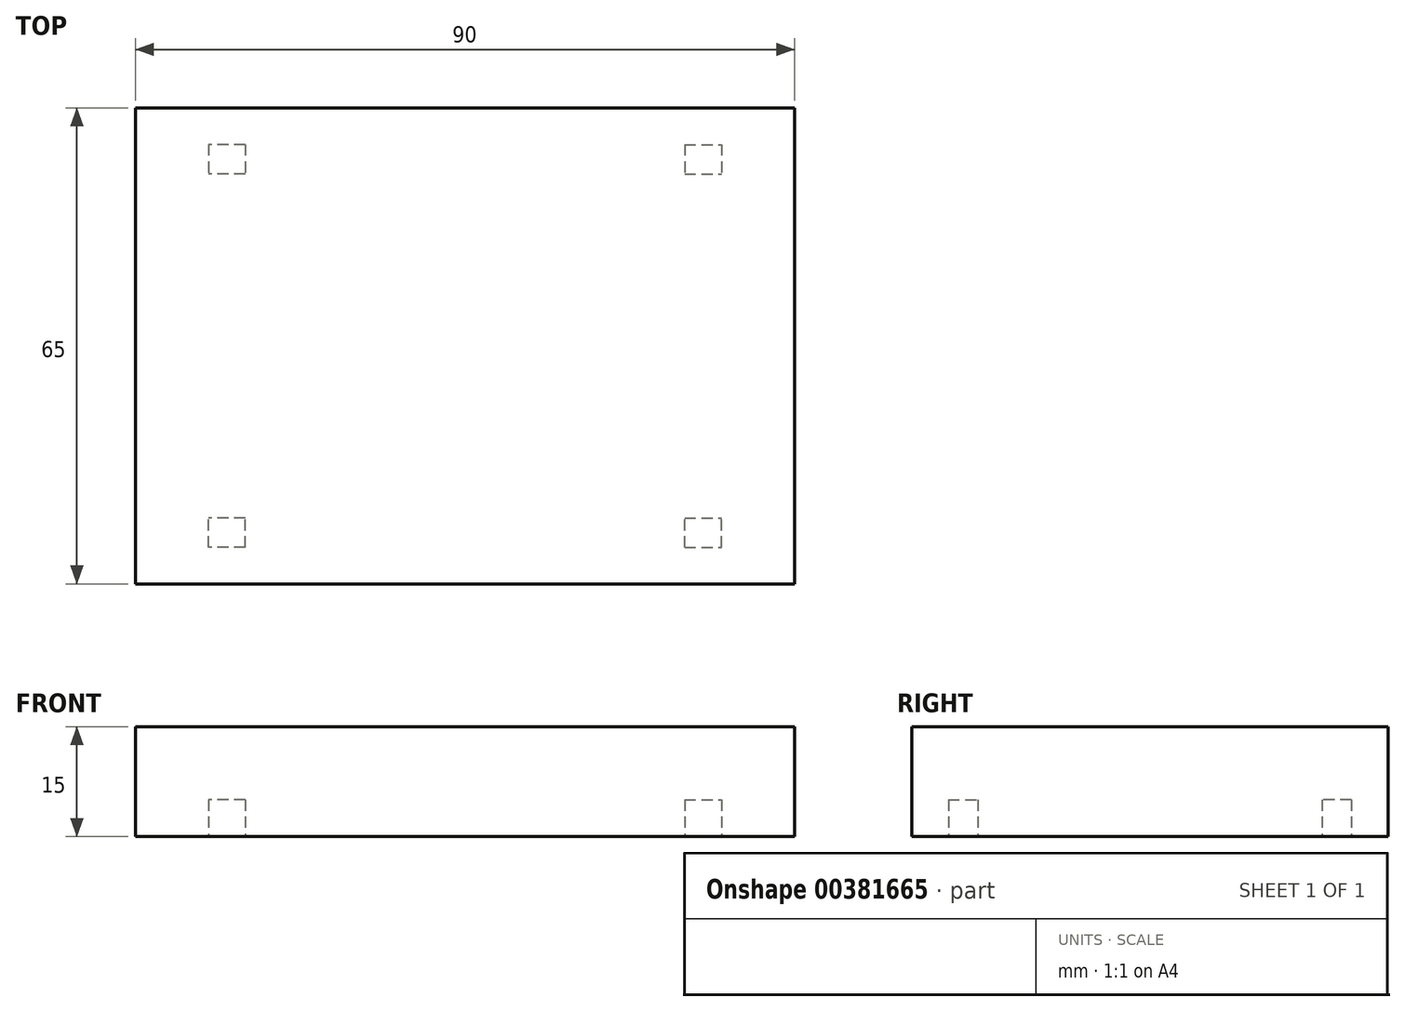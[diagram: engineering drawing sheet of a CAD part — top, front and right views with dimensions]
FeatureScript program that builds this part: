
annotation { "Feature Type Name" : "Feature", "Feature Type Description" : "" }
export const myFeature = defineFeature(function(context is Context, id is Id, definition is map)
    precondition{}
    {
        {
            var Q0;
            Q0=qCreatedBy(makeId("Top.planeOp"),FACE);
            var sketch = newSketch(context, id + "F0", { "sketchPlane" : qUnion([Q0])});
            skLineSegment(sketch, "E0.bottom", {"start": v(-45, 32.5) * mm, "end": v(45, 32.5) * mm});
            skLineSegment(sketch, "E0.top", {"start": v(-45, -32.5) * mm, "end": v(45, -32.5) * mm});
            skLineSegment(sketch, "E0.left", {"start": v(-45, 32.5) * mm, "end": v(-45, -32.5) * mm});
            skLineSegment(sketch, "E0.right", {"start": v(45, 32.5) * mm, "end": v(45, -32.5) * mm});
            skPoint(sketch, "E0.middle", {"position": v(0, 0) * mm});
            skSolve(sketch);
        }
        {
            var Q0;
            Q0 = qSketchRegion(id + "F0", true);
            extrude(context, id + "F1", {"entities" : qUnion([Q0]), "depth" : 15 * mm});
        }
        {
            var Q0;
            Q0=makeQuery(id+"F1.opExtrude","CAP_FACE",FACE,{"disambiguationData":[OSD([sQuery(id+"F0.wireOp",EDGE,"E0.bottom"),sQuery(id+"F0.wireOp",EDGE,"E0.top"),sQuery(id+"F0.wireOp",EDGE,"E0.left"),sQuery(id+"F0.wireOp",EDGE,"E0.right")])],"isStart":true});
            var sketch = newSketch(context, id + "F2", { "sketchPlane" : qUnion([Q0])});
            skLineSegment(sketch, "E1", {"start": v(0, 32.5) * mm, "end": v(30, 32.5) * mm, "construction": true});
            skLineSegment(sketch, "E2", {"start": v(30, 32.5) * mm, "end": v(30, 27.5) * mm, "construction": true});
            skLineSegment(sketch, "E3.bottom", {"start": v(30, 27.5) * mm, "end": v(35, 27.5) * mm});
            skLineSegment(sketch, "E3.top", {"start": v(30, 23.5) * mm, "end": v(35, 23.5) * mm});
            skLineSegment(sketch, "E3.left", {"start": v(30, 27.5) * mm, "end": v(30, 23.5) * mm});
            skLineSegment(sketch, "E3.right", {"start": v(35, 27.5) * mm, "end": v(35, 23.5) * mm});
            skLineSegment(sketch, "E4.bottom", {"start": v(0, 32.5) * mm, "end": v(0, 32.5) * mm});
            skLineSegment(sketch, "E4.top", {"start": v(0, 0) * mm, "end": v(0, 0) * mm});
            skLineSegment(sketch, "E4.left", {"start": v(0, 32.5) * mm, "end": v(0, 0) * mm, "construction": true});
            skLineSegment(sketch, "E4.right", {"start": v(0, 32.5) * mm, "end": v(0, 0) * mm, "construction": true});
            skLineSegment(sketch, "E5.bottom", {"start": v(0, 0) * mm, "end": v(45, 0) * mm, "construction": true});
            skLineSegment(sketch, "E5.top", {"start": v(0, 0) * mm, "end": v(45, 0) * mm, "construction": true});
            skLineSegment(sketch, "E5.right", {"start": v(45, 0) * mm, "end": v(45, 0) * mm});
            skLineSegment(sketch, "E6.MirrorCS", {"start": v(35, -27.5) * mm, "end": v(35, -23.5) * mm});
            skLineSegment(sketch, "E7.MirrorCS", {"start": v(30, -27.5) * mm, "end": v(30, -23.5) * mm});
            skLineSegment(sketch, "E8.MirrorCS", {"start": v(30, -23.5) * mm, "end": v(35, -23.5) * mm});
            skLineSegment(sketch, "E9.MirrorCS", {"start": v(30, -27.5) * mm, "end": v(35, -27.5) * mm});
            skLineSegment(sketch, "E10.MirrorCS", {"start": v(0, -32.5) * mm, "end": v(0, 0) * mm, "construction": true});
            skLineSegment(sketch, "E11.MirrorCS", {"start": v(-35, 27.5) * mm, "end": v(-35, 23.5) * mm});
            skLineSegment(sketch, "E12.MirrorCS", {"start": v(-30, 27.5) * mm, "end": v(-30, 23.5) * mm});
            skLineSegment(sketch, "E13.MirrorCS", {"start": v(-30, 23.5) * mm, "end": v(-35, 23.5) * mm});
            skLineSegment(sketch, "E14.MirrorCS", {"start": v(-30, 27.5) * mm, "end": v(-35, 27.5) * mm});
            skLineSegment(sketch, "E15.MirrorCS", {"start": v(-30, -27.5) * mm, "end": v(-35, -27.5) * mm});
            skLineSegment(sketch, "E16.MirrorCS", {"start": v(-35, -27.5) * mm, "end": v(-35, -23.5) * mm});
            skLineSegment(sketch, "E17.MirrorCS", {"start": v(-30, -27.5) * mm, "end": v(-30, -23.5) * mm});
            skLineSegment(sketch, "E18.MirrorCS", {"start": v(-30, -23.5) * mm, "end": v(-35, -23.5) * mm});
            skSolve(sketch);
        }
        {
            var Q0;
            Q0 = qSketchRegion(id + "F2", true);
            extrude(context, id + "F3", {"entities" : qUnion([Q0]), "operationType" : NewBodyOperationType.REMOVE, "oppositeDirection" : true, "depth" : 5 * mm});
        }
    });
